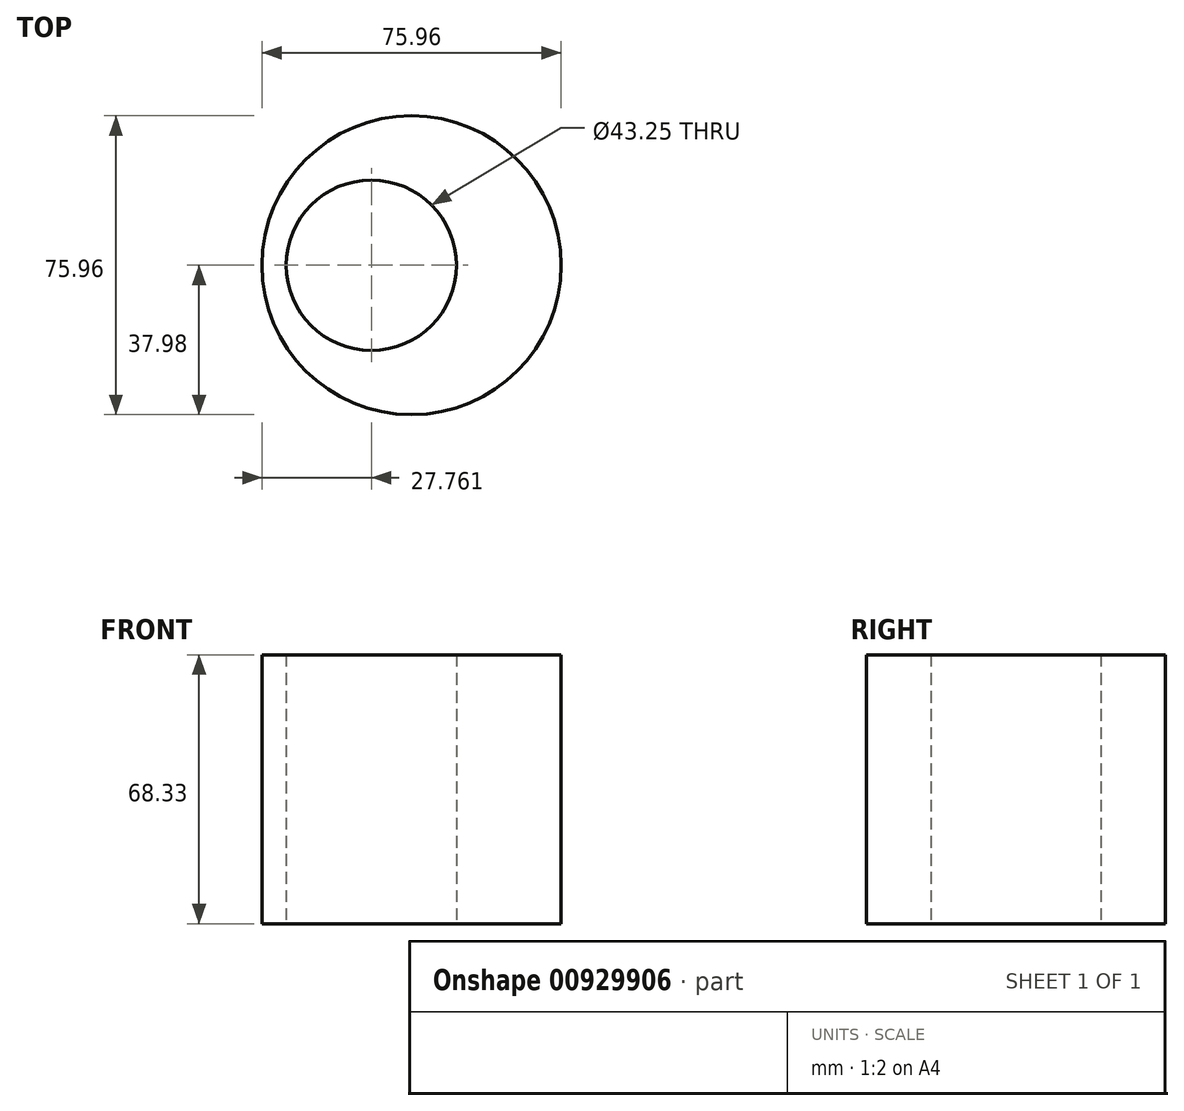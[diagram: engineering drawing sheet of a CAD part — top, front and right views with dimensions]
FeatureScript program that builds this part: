
annotation { "Feature Type Name" : "Feature", "Feature Type Description" : "" }
export const myFeature = defineFeature(function(context is Context, id is Id, definition is map)
    precondition{}
    {
        {
            var Q0;
            Q0=qCreatedBy(makeId("Top.planeOp"),FACE);
            var sketch = newSketch(context, id + "F0", { "sketchPlane" : qUnion([Q0])});
            skCircle(sketch, "E0", {"center": v(-10.22, 0) * mm, "radius": 21.63 * mm});
            skCircle(sketch, "E1", {"center": v(0, 0) * mm, "radius": 37.98 * mm});
            skSolve(sketch);
        }
        {
            var Q0;
            Q0 = qSketchRegion(id + "F0", true);
            extrude(context, id + "F1", {"entities" : qUnion([Q0]), "depth" : 42.93 * mm, "offsetDistance" : 25.4 * mm});
        }
        {
            var Q0;
            Q0=makeQuery(id+"F1.opExtrude","CAP_FACE",FACE,{"disambiguationData":[OSD([sQuery(id+"F0.wireOp",EDGE,"E0"),sQuery(id+"F0.wireOp",EDGE,"E1")])],"isStart":false});
            extrude(context, id + "F2", {"entities" : qUnion([Q0]), "operationType" : NewBodyOperationType.REMOVE, "depth" : 14.22 * mm, "offsetDistance" : 25.4 * mm});
        }
        {
            var Q0;
            Q0=makeQuery(id+"F1.opExtrude","CAP_FACE",FACE,{"disambiguationData":[OSD([sQuery(id+"F0.wireOp",EDGE,"E0"),sQuery(id+"F0.wireOp",EDGE,"E1")])],"isStart":false});
            extrude(context, id + "F3", {"entities" : qUnion([Q0]), "operationType" : NewBodyOperationType.ADD, "depth" : 25.4 * mm, "offsetDistance" : 25.4 * mm});
        }
    });
